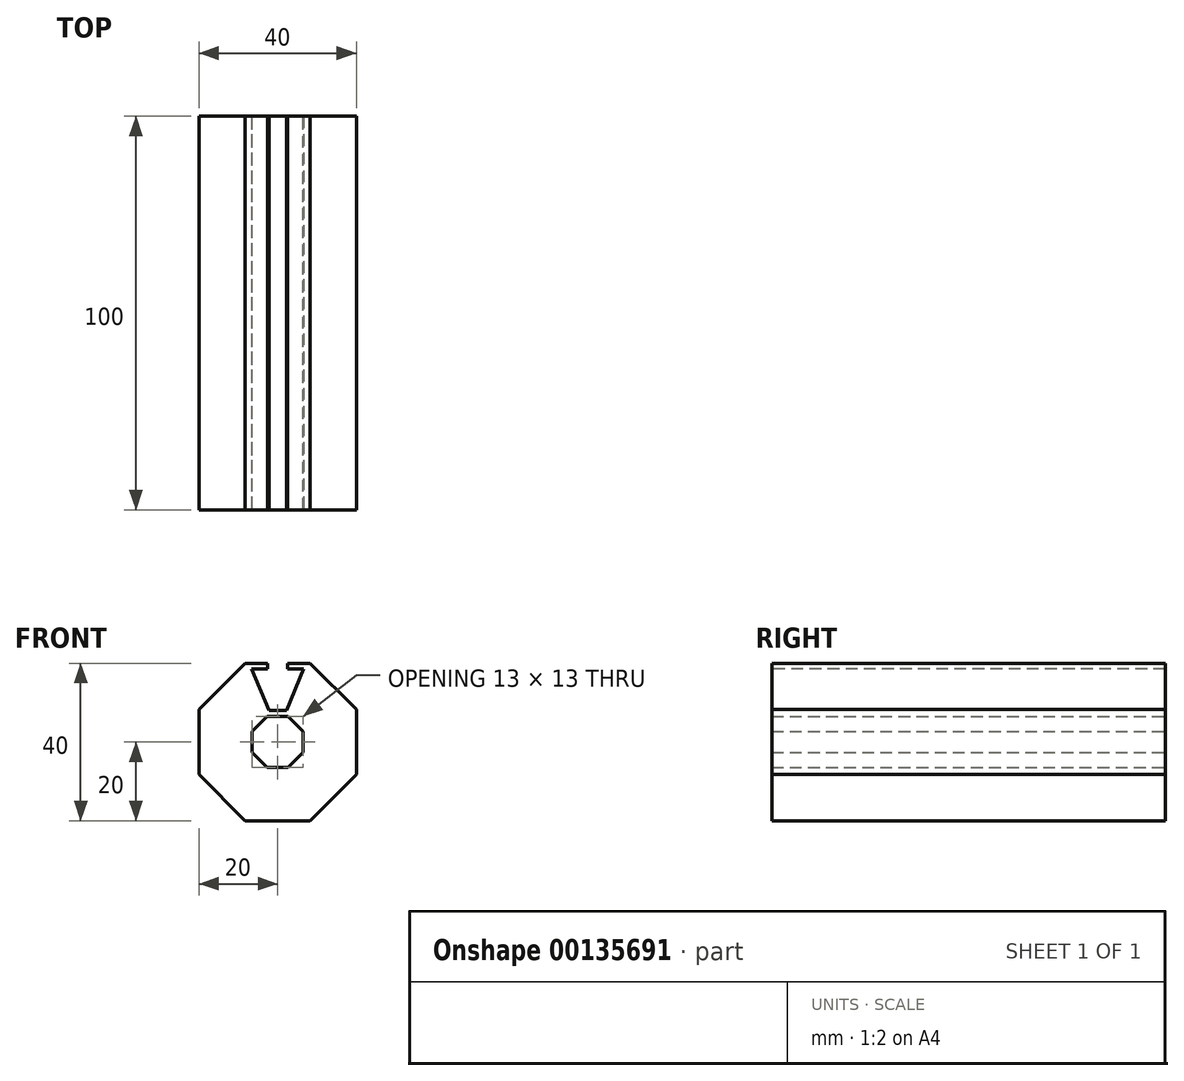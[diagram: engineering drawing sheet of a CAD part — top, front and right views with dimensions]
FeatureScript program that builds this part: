
annotation { "Feature Type Name" : "Feature", "Feature Type Description" : "" }
export const myFeature = defineFeature(function(context is Context, id is Id, definition is map)
    precondition{}
    {
        {
            var Q0;
            Q0=qCreatedBy(makeId("Front.planeOp"),FACE);
            var sketch = newSketch(context, id + "F0", { "sketchPlane" : qUnion([Q0])});
            skCircle(sketch, "E0.cCircle", {"center": v(0, 0) * mm, "radius": 20 * mm, "construction": true});
            skLineSegment(sketch, "E0.0", {"start": v(-8.28, 20) * mm, "end": v(8.28, 20) * mm});
            skLineSegment(sketch, "E0.1", {"start": v(8.28, 20) * mm, "end": v(20, 8.28) * mm});
            skLineSegment(sketch, "E0.2", {"start": v(20, 8.28) * mm, "end": v(20, -8.28) * mm});
            skLineSegment(sketch, "E0.3", {"start": v(20, -8.28) * mm, "end": v(8.28, -20) * mm});
            skLineSegment(sketch, "E0.4", {"start": v(8.28, -20) * mm, "end": v(-8.28, -20) * mm});
            skLineSegment(sketch, "E0.5", {"start": v(-8.28, -20) * mm, "end": v(-20, -8.28) * mm});
            skLineSegment(sketch, "E0.6", {"start": v(-20, -8.28) * mm, "end": v(-20, 8.28) * mm});
            skLineSegment(sketch, "E0.7", {"start": v(-20, 8.28) * mm, "end": v(-8.28, 20) * mm});
            skPoint(sketch, "E0.0.midPoint", {"position": v(0, 20) * mm});
            skCircle(sketch, "E1.cCircle", {"center": v(0, 0) * mm, "radius": 6.5 * mm, "construction": true});
            skLineSegment(sketch, "E1.0", {"start": v(-2.7, 6.5) * mm, "end": v(2.7, 6.5) * mm});
            skLineSegment(sketch, "E1.1", {"start": v(2.7, 6.5) * mm, "end": v(6.5, 2.7) * mm});
            skLineSegment(sketch, "E1.2", {"start": v(6.5, 2.7) * mm, "end": v(6.5, -2.7) * mm});
            skLineSegment(sketch, "E1.3", {"start": v(6.5, -2.7) * mm, "end": v(2.7, -6.5) * mm});
            skLineSegment(sketch, "E1.4", {"start": v(2.7, -6.5) * mm, "end": v(-2.7, -6.5) * mm});
            skLineSegment(sketch, "E1.5", {"start": v(-2.7, -6.5) * mm, "end": v(-6.5, -2.7) * mm});
            skLineSegment(sketch, "E1.6", {"start": v(-6.5, -2.7) * mm, "end": v(-6.5, 2.7) * mm});
            skLineSegment(sketch, "E1.7", {"start": v(-6.5, 2.7) * mm, "end": v(-2.7, 6.5) * mm});
            skPoint(sketch, "E1.0.midPoint", {"position": v(0, 6.5) * mm});
            skSolve(sketch);
        }
        {
            var Q0;
            Q0 = qSketchRegion(id + "F0", true);
            extrude(context, id + "F1", {"entities" : qUnion([Q0]), "depth" : 100 * mm});
        }
        {
            var Q0;
            Q0=makeQuery(id+"F1.opExtrude","CAP_FACE",FACE,{"disambiguationData":[OSD([sQuery(id+"F0.wireOp",EDGE,"E0.0"),sQuery(id+"F0.wireOp",EDGE,"E0.1"),sQuery(id+"F0.wireOp",EDGE,"E0.2"),sQuery(id+"F0.wireOp",EDGE,"E0.3"),sQuery(id+"F0.wireOp",EDGE,"E0.4"),sQuery(id+"F0.wireOp",EDGE,"E0.5"),sQuery(id+"F0.wireOp",EDGE,"E0.6"),sQuery(id+"F0.wireOp",EDGE,"E0.7"),sQuery(id+"F0.wireOp",EDGE,"E1.0"),sQuery(id+"F0.wireOp",EDGE,"E1.1"),sQuery(id+"F0.wireOp",EDGE,"E1.2"),sQuery(id+"F0.wireOp",EDGE,"E1.3"),sQuery(id+"F0.wireOp",EDGE,"E1.4"),sQuery(id+"F0.wireOp",EDGE,"E1.5"),sQuery(id+"F0.wireOp",EDGE,"E1.6"),sQuery(id+"F0.wireOp",EDGE,"E1.7")])],"isStart":false});
            var sketch = newSketch(context, id + "F2", { "sketchPlane" : qUnion([Q0])});
            skLineSegment(sketch, "E2", {"start": v(-3.31, 8) * mm, "end": v(-7.66, 18.5) * mm});
            skLineSegment(sketch, "E3", {"start": v(3.31, 8) * mm, "end": v(7.66, 18.5) * mm});
            skLineSegment(sketch, "E4", {"start": v(7.66, 18.5) * mm, "end": v(-7.66, 18.5) * mm});
            skLineSegment(sketch, "E5", {"start": v(3.31, 8) * mm, "end": v(-3.31, 8) * mm});
            skLineSegment(sketch, "E6.0", {"start": v(2.23, 8) * mm, "end": v(6.58, 18.5) * mm});
            skLineSegment(sketch, "E7.0", {"start": v(-2.23, 8) * mm, "end": v(-6.58, 18.5) * mm});
            skSolve(sketch);
        }
        {
            var Q0;
            {var subQ0=sQuery(id+"F2.wireOp",EDGE,"E6.0");Q0=makeQuery(id+"F2.imprint","IMPRINT",FACE,{"disambiguationData":[TD([[makeQuery(id+"F2.imprint","IMPRINT",EDGE,{"derivedFrom":subQ0}),1.0]])]});}
            extrude(context, id + "F3", {"entities" : qUnion([Q0]), "operationType" : NewBodyOperationType.REMOVE, "endBound" : BoundingType.THROUGH_ALL, "oppositeDirection" : true, "depth" : 25.4 * mm});
        }
        {
            var Q0;
            Q0=makeQuery(id+"F1.opExtrude","CAP_FACE",FACE,{"disambiguationData":[OSD([sQuery(id+"F0.wireOp",EDGE,"E0.0"),sQuery(id+"F0.wireOp",EDGE,"E0.1"),sQuery(id+"F0.wireOp",EDGE,"E0.2"),sQuery(id+"F0.wireOp",EDGE,"E0.3"),sQuery(id+"F0.wireOp",EDGE,"E0.4"),sQuery(id+"F0.wireOp",EDGE,"E0.5"),sQuery(id+"F0.wireOp",EDGE,"E0.6"),sQuery(id+"F0.wireOp",EDGE,"E0.7"),sQuery(id+"F0.wireOp",EDGE,"E1.0"),sQuery(id+"F0.wireOp",EDGE,"E1.1"),sQuery(id+"F0.wireOp",EDGE,"E1.2"),sQuery(id+"F0.wireOp",EDGE,"E1.3"),sQuery(id+"F0.wireOp",EDGE,"E1.4"),sQuery(id+"F0.wireOp",EDGE,"E1.5"),sQuery(id+"F0.wireOp",EDGE,"E1.6"),sQuery(id+"F0.wireOp",EDGE,"E1.7")])],"isStart":false});
            var sketch = newSketch(context, id + "F4", { "sketchPlane" : qUnion([Q0])});
            skLineSegment(sketch, "E8", {"start": v(-2.5, 20) * mm, "end": v(-2.5, 18.5) * mm});
            skLineSegment(sketch, "E9", {"start": v(2.5, 20) * mm, "end": v(2.5, 18.5) * mm});
            skLineSegment(sketch, "E10", {"start": v(0, 18.5) * mm, "end": v(0, 20) * mm, "construction": true});
            skLineSegment(sketch, "E11", {"start": v(-2.5, 20) * mm, "end": v(2.5, 20) * mm});
            skLineSegment(sketch, "E12", {"start": v(2.5, 18.5) * mm, "end": v(-2.5, 18.5) * mm});
            skSolve(sketch);
        }
        {
            var Q0;
            Q0 = qSketchRegion(id + "F4", true);
            extrude(context, id + "F5", {"entities" : qUnion([Q0]), "operationType" : NewBodyOperationType.REMOVE, "endBound" : BoundingType.THROUGH_ALL, "oppositeDirection" : true, "depth" : 25.4 * mm});
        }
        {
            var Q0;
            Q0=qCreatedBy(makeId("Right.planeOp"),FACE);
            var sketch = newSketch(context, id + "F6", { "sketchPlane" : qUnion([Q0])});
            skLineSegment(sketch, "E13", {"start": v(0, 0) * mm, "end": v(-108.19, 0) * mm});
            skSolve(sketch);
        }
    });
